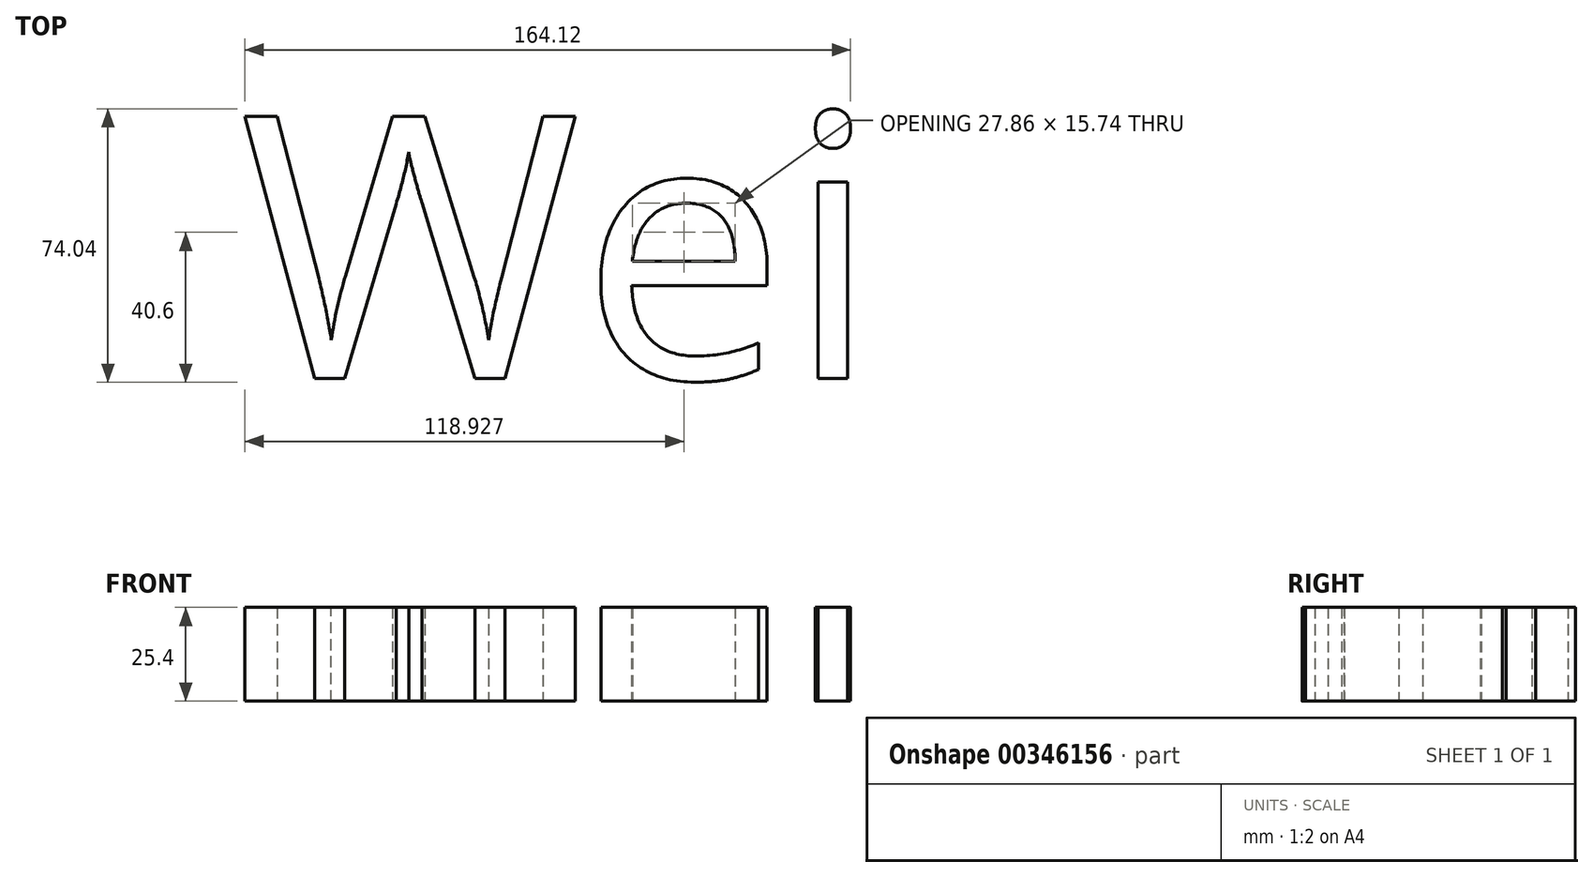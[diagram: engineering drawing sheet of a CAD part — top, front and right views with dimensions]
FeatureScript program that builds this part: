
annotation { "Feature Type Name" : "Feature", "Feature Type Description" : "" }
export const myFeature = defineFeature(function(context is Context, id is Id, definition is map)
    precondition{}
    {
        {
            var Q0;
            Q0=qCreatedBy(makeId("Top.planeOp"),FACE);
            var sketch = newSketch(context, id + "F0", { "sketchPlane" : qUnion([Q0])});
            skText(sketch, "E0", { "text": "Wei", "fontName": "OpenSans-Regular.ttf"});
            const initialGuessF0  = {"E0": [-0.06418, -0.01112, 1, 0, 0.07168]};
            skSetInitialGuess(sketch, initialGuessF0);
            skSolve(sketch);
        }
        {
            var Q0;
            Q0 = qSketchRegion(id + "F0", true);
            extrude(context, id + "F1", {"entities" : qUnion([Q0]), "depth" : 25.4 * mm});
        }
    });
